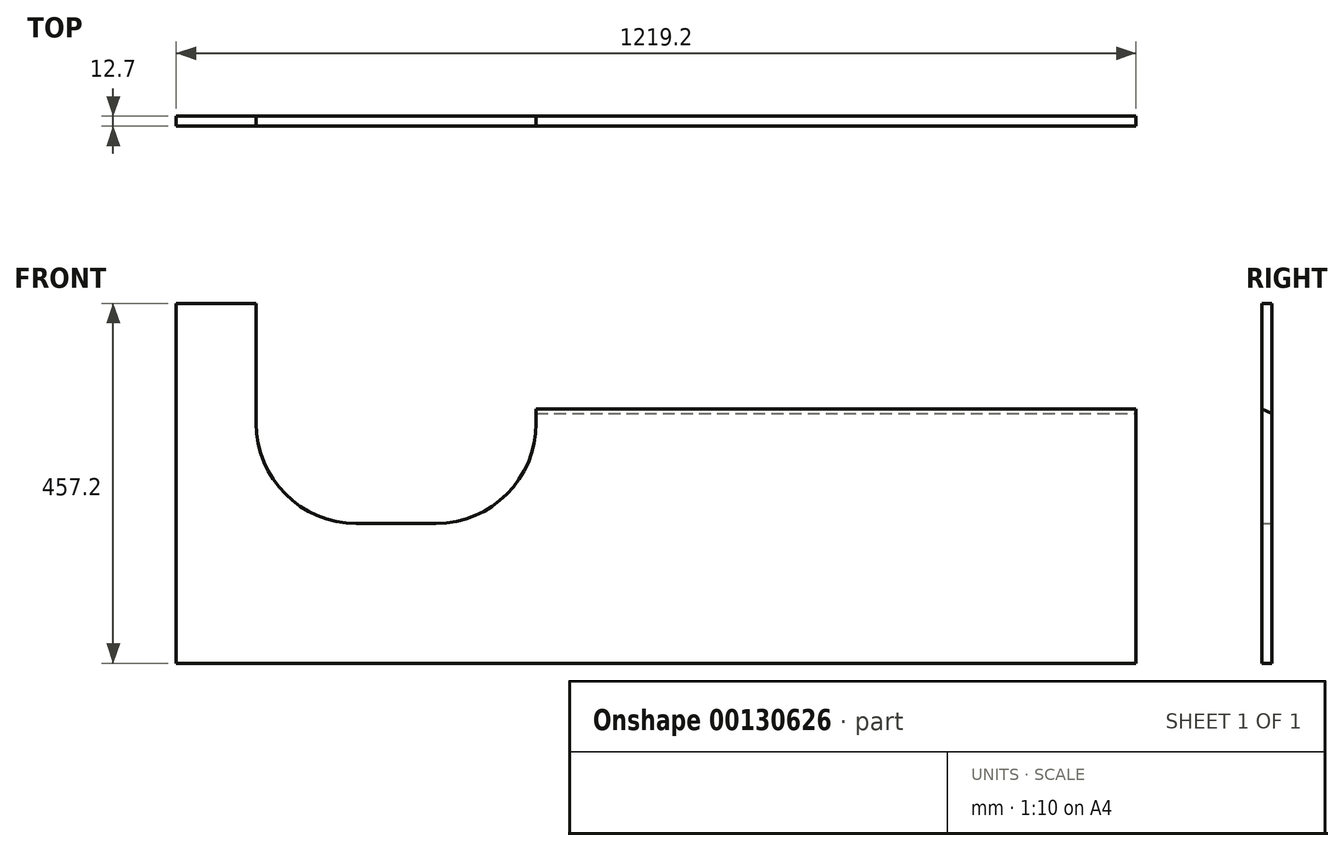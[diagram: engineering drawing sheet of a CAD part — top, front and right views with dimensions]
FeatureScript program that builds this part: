
annotation { "Feature Type Name" : "Feature", "Feature Type Description" : "" }
export const myFeature = defineFeature(function(context is Context, id is Id, definition is map)
    precondition{}
    {
        {
            var Q0;
            Q0=qCreatedBy(makeId("Front.planeOp"),FACE);
            var sketch = newSketch(context, id + "F0", { "sketchPlane" : qUnion([Q0])});
            skLineSegment(sketch, "E0.bottom", {"start": v(0, 0) * mm, "end": v(762, 0) * mm});
            skLineSegment(sketch, "E0.top", {"start": v(0, 317.5) * mm, "end": v(762, 317.5) * mm});
            skLineSegment(sketch, "E0.left", {"start": v(0, 304.8) * mm, "end": v(0, 317.5) * mm});
            skLineSegment(sketch, "E0.right", {"start": v(762, 0) * mm, "end": v(762, 317.5) * mm});
            skLineSegment(sketch, "E1.bottom", {"start": v(0, 0) * mm, "end": v(-457.2, 0) * mm});
            skLineSegment(sketch, "E2.top", {"start": v(-457.2, 457.2) * mm, "end": v(-355.6, 457.2) * mm});
            skLineSegment(sketch, "E2.left", {"start": v(-457.2, 0) * mm, "end": v(-457.2, 457.2) * mm});
            skLineSegment(sketch, "E2.right", {"start": v(-355.6, 304.8) * mm, "end": v(-355.6, 457.2) * mm});
            skLineSegment(sketch, "E3.bottom", {"start": v(-457.2, 0) * mm, "end": v(0, 0) * mm});
            skLineSegment(sketch, "E3.top", {"start": v(-228.6, 177.8) * mm, "end": v(-127, 177.8) * mm});
            skPoint(sketch, "E4.visualSharp", {"position": v(-355.6, 177.8) * mm});
            skArc(sketch, "E4.filletArc", {"start": v(-355.6, 304.8) * mm, "mid": v(-318.4, 215) * mm, "end": v(-228.6, 177.8) * mm});
            skPoint(sketch, "E5.visualSharp", {"position": v(0, 177.8) * mm});
            skArc(sketch, "E5.filletArc", {"start": v(-127, 177.8) * mm, "mid": v(-37.2, 215) * mm, "end": v(0, 304.8) * mm});
            skSolve(sketch);
        }
        {
            var Q0;
            Q0=makeQuery(id+"F0.imprint","IMPRINT",FACE,{"disambiguationData":[TD([[makeQuery(id+"F0.imprint","IMPRINT",EDGE,{"derivedFrom":sQuery(id+"F0.wireOp",EDGE,"E0.bottom")}),1.0]])]});
            var Q1;
            {var subQ0=sQuery(id+"F0.wireOp",EDGE,"E2.top");Q1=makeQuery(id+"F0.imprint","IMPRINT",FACE,{"disambiguationData":[TD([[makeQuery(id+"F0.imprint","IMPRINT",EDGE,{"derivedFrom":subQ0}),-1.0]])]});}
            var Q2;
            {var subQ5=sQuery(id+"F0.wireOp",EDGE,"E3.left");Q2=makeQuery(id+"F0.imprint","IMPRINT",FACE,{"disambiguationData":[TD([[makeQuery(id+"F0.imprint","IMPRINT",EDGE,{"derivedFrom":subQ5}),-1.0]])]});}
            var Q3;
            {var subQ5=sQuery(id+"F0.wireOp",EDGE,"E3.right");Q3=makeQuery(id+"F0.imprint","IMPRINT",FACE,{"disambiguationData":[TD([[makeQuery(id+"F0.imprint","IMPRINT",EDGE,{"derivedFrom":subQ5}),1.0]])]});}
            extrude(context, id + "F1", {"entities" : qUnion([Q0, Q1, Q2, Q3]), "depth" : 12.7 * mm});
        }
        {
            var Q0;
            Q0=makeQuery(id+"F1.opExtrude","SWEPT_FACE",FACE,{"disambiguationData":[OSD([sQuery(id+"F0.wireOp",EDGE,"E0.right")])]});
            var sketch = newSketch(context, id + "F2", { "sketchPlane" : qUnion([Q0])});
            skLineSegment(sketch, "E6", {"start": v(0, 317.5) * mm, "end": v(-12.7, 317.5) * mm});
            skLineSegment(sketch, "E7", {"start": v(-12.7, 317.5) * mm, "end": v(-12.7, 322.76) * mm});
            skLineSegment(sketch, "E8", {"start": v(-12.7, 322.76) * mm, "end": v(0, 317.5) * mm});
            skSolve(sketch);
        }
        {
            var Q0;
            Q0=makeQuery(id+"F2.imprint","IMPRINT",FACE,{"disambiguationData":[TD([[makeQuery(id+"F2.imprint","IMPRINT",EDGE,{"derivedFrom":sQuery(id+"F2.wireOp",EDGE,"E6")}),1.0]])]});
            var Q1;
            Q1=makeQuery(id+"F1.opExtrude","SWEPT_FACE",FACE,{"disambiguationData":[OSD([sQuery(id+"F0.wireOp",EDGE,"E0.left")])]});
            extrude(context, id + "F3", {"entities" : qUnion([Q0]), "operationType" : NewBodyOperationType.ADD, "endBound" : BoundingType.UP_TO_SURFACE, "oppositeDirection" : true, "endBoundEntityFace" : qUnion([Q1]), "depth" : 25.4 * mm});
        }
    });
